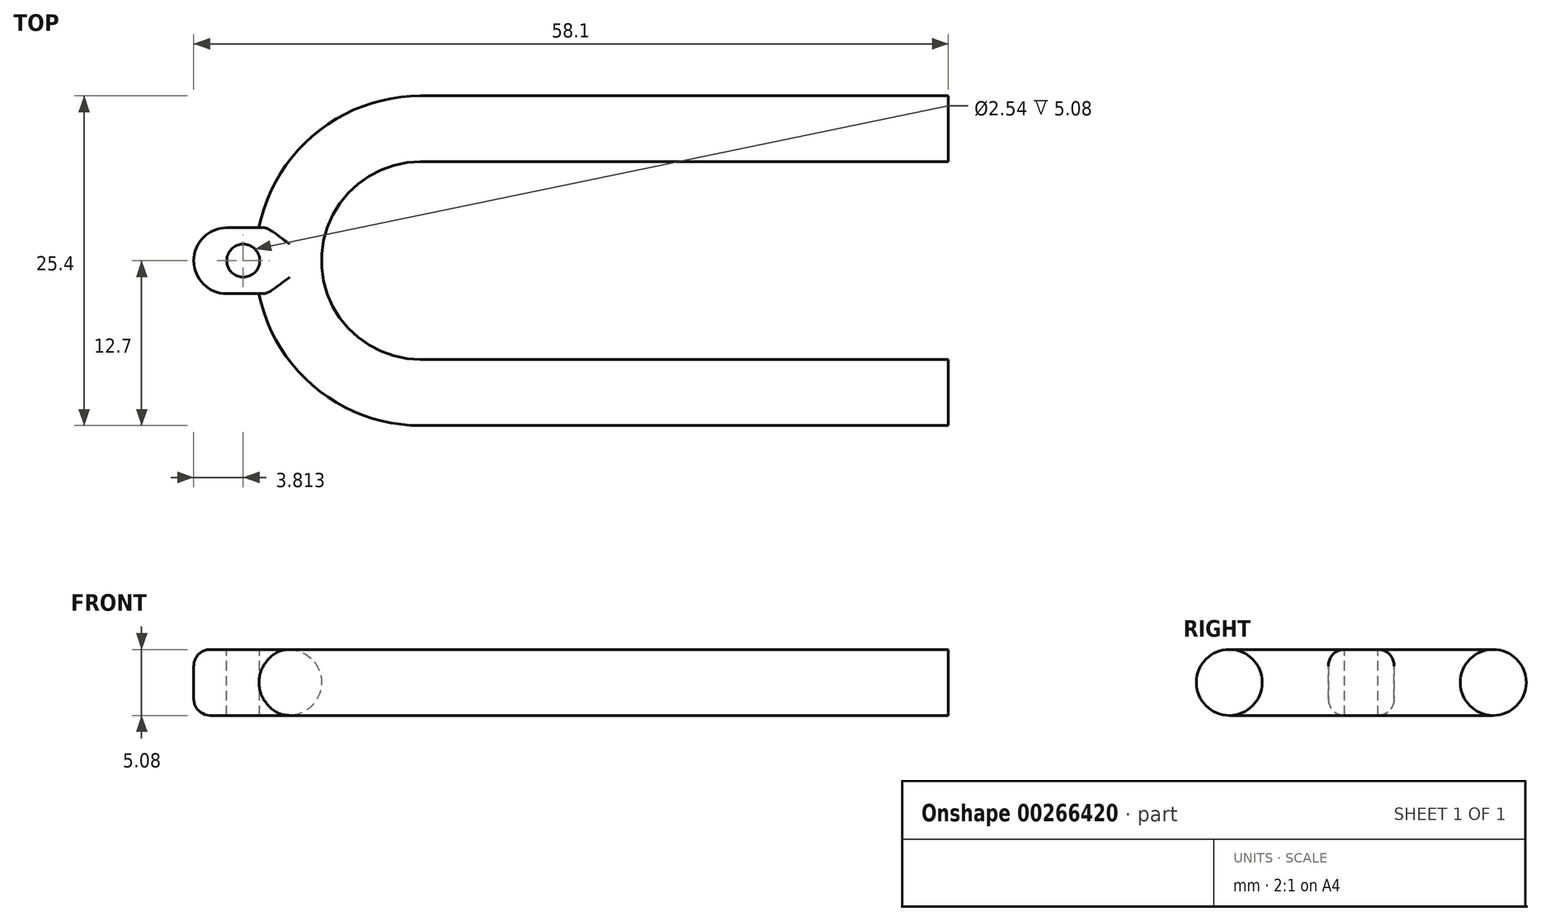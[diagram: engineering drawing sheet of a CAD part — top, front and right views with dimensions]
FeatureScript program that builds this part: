
annotation { "Feature Type Name" : "Feature", "Feature Type Description" : "" }
export const myFeature = defineFeature(function(context is Context, id is Id, definition is map)
    precondition{}
    {
        {
            var Q0;
            Q0=qCreatedBy(makeId("Top.planeOp"),FACE);
            var sketch = newSketch(context, id + "F0", { "sketchPlane" : qUnion([Q0])});
            skLineSegment(sketch, "E0.bottom", {"start": v(10.16, 20.32) * mm, "end": v(50.8, 20.32) * mm});
            skLineSegment(sketch, "E0.top", {"start": v(10.16, 0) * mm, "end": v(50.8, 0) * mm});
            skLineSegment(sketch, "E0.left", {"start": v(0, 10.16) * mm, "end": v(0, 10.16) * mm});
            skPoint(sketch, "E1.visualSharp", {"position": v(0, 20.32) * mm});
            skArc(sketch, "E1.filletArc", {"start": v(10.16, 20.32) * mm, "mid": v(2.98, 17.34) * mm, "end": v(0, 10.16) * mm});
            skPoint(sketch, "E2.visualSharp", {"position": v(0, 0) * mm});
            skArc(sketch, "E2.filletArc", {"start": v(0, 10.16) * mm, "mid": v(2.98, 2.98) * mm, "end": v(10.16, 0) * mm});
            skPoint(sketch, "E3", {"position": v(0, 10.16) * mm});
            skLineSegment(sketch, "E4", {"start": v(0, 10.16) * mm, "end": v(50.8, 10.16) * mm, "construction": true});
            skLineSegment(sketch, "E5.bottom", {"start": v(0.32, 12.7) * mm, "end": v(-7.3, 12.7) * mm});
            skLineSegment(sketch, "E5.top", {"start": v(0.32, 7.62) * mm, "end": v(-7.3, 7.62) * mm});
            skLineSegment(sketch, "E5.left", {"start": v(0.32, 12.7) * mm, "end": v(0.32, 7.62) * mm});
            skLineSegment(sketch, "E5.right", {"start": v(-7.3, 12.7) * mm, "end": v(-7.3, 7.62) * mm});
            skSolve(sketch);
        }
        {
            var Q0;
            Q0=qCreatedBy(makeId("Right.planeOp"),FACE);
            cPlane(context, id + "F1", {"entities" : qUnion([Q0]), "cplaneType" : CPlaneType.OFFSET, "offset" : 50.8 * mm, "width" : 152.4 * mm, "height" : 152.4 * mm});
        }
        {
            var Q0;
            Q0=qCreatedBy(id+"F1.planeOp",FACE);
            var sketch = newSketch(context, id + "F2", { "sketchPlane" : qUnion([Q0])});
            skCircle(sketch, "E6", {"center": v(0, 0) * mm, "radius": 2.54 * mm});
            skSolve(sketch);
        }
        {
            var Q0;
            Q0=makeQuery(id+"F2.imprint","IMPRINT",FACE,{"disambiguationData":[TD([[makeQuery(id+"F2.imprint","IMPRINT",EDGE,{"derivedFrom":sQuery(id+"F2.wireOp",EDGE,"E6")}),1.0]])]});
            var Q1;
            Q1=sQuery(id+"F0.wireOp",EDGE,"E0.top");
            var Q2;
            Q2=sQuery(id+"F0.wireOp",EDGE,"E2.filletArc");
            var Q3;
            Q3=sQuery(id+"F0.wireOp",EDGE,"E1.filletArc");
            var Q4;
            Q4=sQuery(id+"F0.wireOp",EDGE,"E0.bottom");
            sweep(context, id + "F3", {"profiles" : qUnion([Q0]), "path" : qUnion([Q1, Q2, Q3, Q4])});
        }
        {
            var Q0;
            Q0=qCreatedBy(makeId("Top.planeOp"),FACE);
            cPlane(context, id + "F4", {"entities" : qUnion([Q0]), "cplaneType" : CPlaneType.OFFSET, "offset" : 2.54 * mm, "width" : 152.4 * mm, "height" : 152.4 * mm});
        }
        {
            var Q0;
            {var subQ1=sQuery(id+"F0.wireOp",EDGE,"E5.bottom");Q0=makeQuery(id+"F0.imprint","IMPRINT",FACE,{"disambiguationData":[TD([[makeQuery(id+"F0.imprint","IMPRINT",EDGE,{"derivedFrom":subQ1}),1.0]])]});}
            extrude(context, id + "F5", {"entities" : qUnion([Q0]), "operationType" : NewBodyOperationType.ADD, "depth" : 2.54 * mm, "hasSecondDirection" : true, "secondDirectionOppositeDirection" : true, "secondDirectionDepth" : 2.54 * mm});
        }
        {
            var Q0;
            Q0=makeQuery(id+"F5.opExtrude","SWEPT_EDGE",EDGE,{"disambiguationData":[OSD([sQuery(id+"F0.wireOp",EDGE,"E5.bottom"),sQuery(id+"F0.wireOp",EDGE,"E5.right")])]});
            var Q1;
            Q1=makeQuery(id+"F5.opExtrude","SWEPT_EDGE",EDGE,{"disambiguationData":[OSD([sQuery(id+"F0.wireOp",EDGE,"E5.top"),sQuery(id+"F0.wireOp",EDGE,"E5.right")])]});
            fillet(context, id + "F6", {"entities" : qUnion([Q0, Q1]), "radius" : 2.54 * mm, "tangentPropagation" : true, "allowEdgeOverflow" : false});
        }
        {
            var Q0;
            Q0=makeQuery(id+"F5.opExtrude","CAP_EDGE",EDGE,{"disambiguationData":[OSD([sQuery(id+"F0.wireOp",EDGE,"E5.bottom")])],"isStart":false});
            var Q1;
            Q1=makeQuery(id+"F5.opExtrude","CAP_EDGE",EDGE,{"disambiguationData":[OSD([sQuery(id+"F0.wireOp",EDGE,"E5.top")])],"isStart":false});
            var Q2;
            {var subQ0=sQuery(id+"F0.wireOp",EDGE,"E5.right");var subQ1=sQuery(id+"F0.wireOp",EDGE,"E5.top");Q2=makeQuery(id+"F6.opFillet","BLEND_EDGE",EDGE,{"blendedFrom":[makeQuery(id+"F5.opExtrude","SWEPT_EDGE",EDGE,{"disambiguationData":[OSD([subQ1,subQ0])]}),makeQuery(id+"F5.opExtrude","CAP_FACE",FACE,{"disambiguationData":[OSD([sQuery(id+"F0.wireOp",EDGE,"E1.filletArc"),sQuery(id+"F0.wireOp",EDGE,"E2.filletArc"),sQuery(id+"F0.wireOp",EDGE,"E5.bottom"),subQ1,subQ0])],"isStart":true})],"blendedInto":[makeQuery(id+"F5.opExtrude","CAP_FACE",FACE,{"disambiguationData":[OSD([sQuery(id+"F0.wireOp",EDGE,"E1.filletArc"),sQuery(id+"F0.wireOp",EDGE,"E2.filletArc"),sQuery(id+"F0.wireOp",EDGE,"E5.bottom"),subQ1,subQ0])],"isStart":true})]});}
            var Q3;
            Q3=makeQuery(id+"F5.opExtrude","CAP_EDGE",EDGE,{"disambiguationData":[OSD([sQuery(id+"F0.wireOp",EDGE,"E5.bottom")])],"isStart":true});
            fillet(context, id + "F7", {"entities" : qUnion([Q0, Q1, Q2, Q3]), "radius" : 1.27 * mm, "tangentPropagation" : true, "allowEdgeOverflow" : false});
        }
        {
            var Q0;
            Q0=makeQuery(id+"F5.opExtrude","CAP_FACE",FACE,{"disambiguationData":[OSD([sQuery(id+"F0.wireOp",EDGE,"E1.filletArc"),sQuery(id+"F0.wireOp",EDGE,"E2.filletArc"),sQuery(id+"F0.wireOp",EDGE,"E5.bottom"),sQuery(id+"F0.wireOp",EDGE,"E5.top"),sQuery(id+"F0.wireOp",EDGE,"E5.right")])],"isStart":false});
            var sketch = newSketch(context, id + "F8", { "sketchPlane" : qUnion([Q0])});
            skCircle(sketch, "E7", {"center": v(-3.49, 10.16) * mm, "radius": 1.27 * mm});
            skPoint(sketch, "E7.centerSnap0", {"position": v(-6.03, 10.16) * mm});
            skSolve(sketch);
        }
        {
            var Q0;
            Q0 = qSketchRegion(id + "F8", true);
            extrude(context, id + "F9", {"entities" : qUnion([Q0]), "operationType" : NewBodyOperationType.REMOVE, "oppositeDirection" : true, "depth" : 25.4 * mm});
        }
    });
